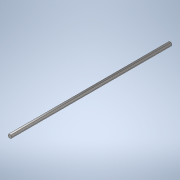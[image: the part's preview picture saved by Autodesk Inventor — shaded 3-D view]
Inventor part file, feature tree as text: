
AUTODESK INVENTOR PART (.ipt)
format: ipt  version: 2020 (Build 240168000, 168)  size: 107,008 bytes
history: native  units: in
note: dims shown in document units (in); Inventor stores cm internally (conversion verified against a paired STEP export)
features: extrude x1, sketch x1
ambient origin geometry x8: Origin, YZ Plane, XZ Plane, XY Plane, X Axis, Y Axis, Z Axis, Center Point
bodies: Solid1 (feature_tree)
feature tree (2):
  extrude  "Extrusion1"  Depth=25.0in TaperAngle=0.0deg
  sketch  "Sketch1"  dims[d0=0.5in d1=25.0in d2=0.0in]
